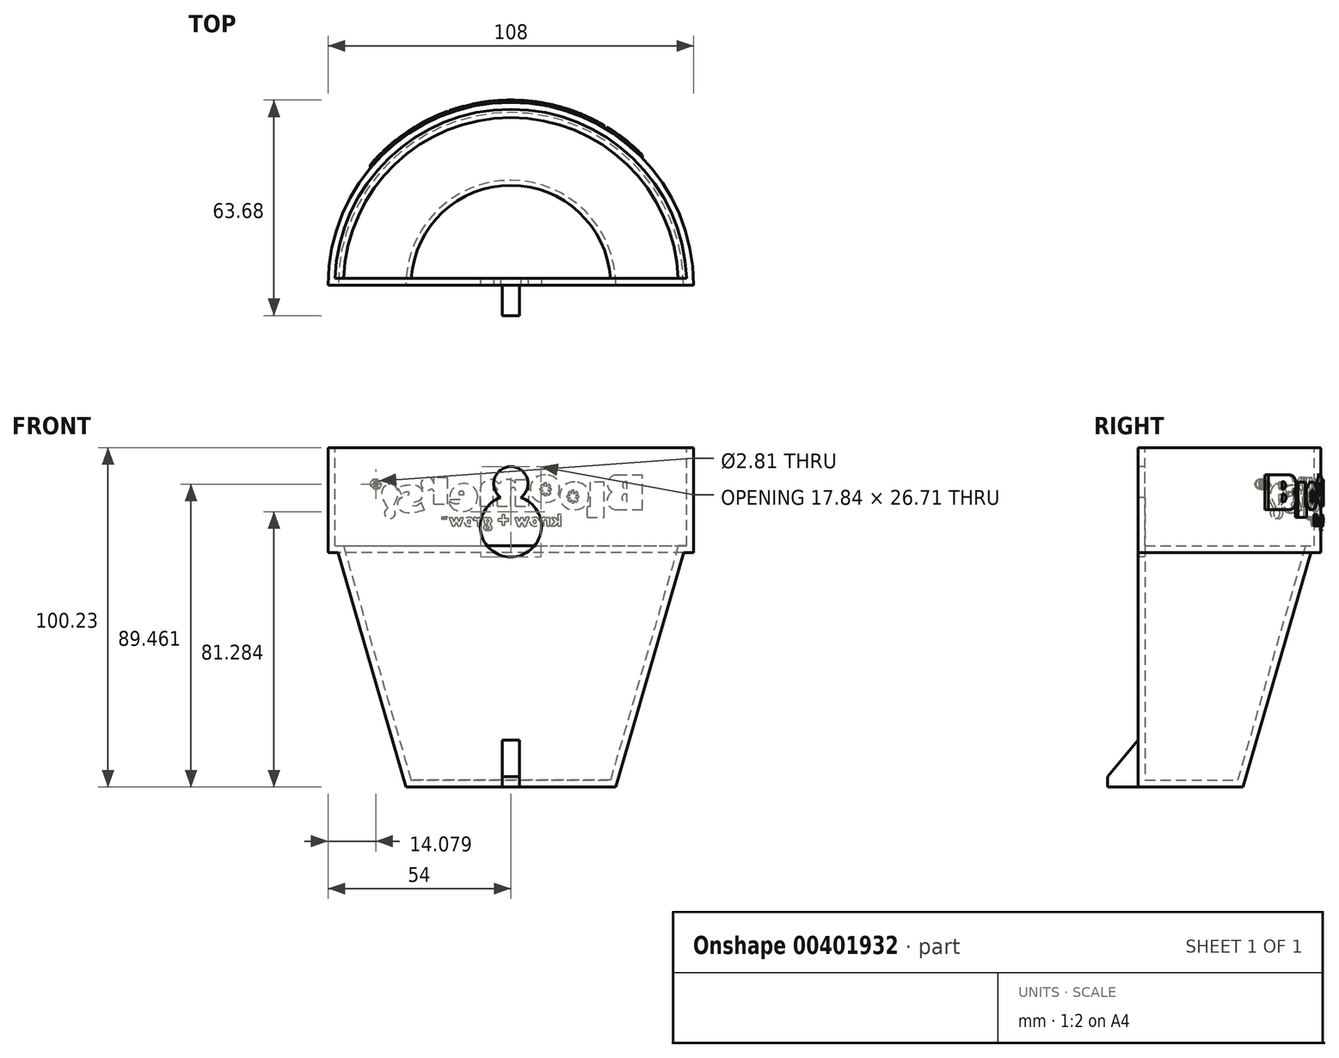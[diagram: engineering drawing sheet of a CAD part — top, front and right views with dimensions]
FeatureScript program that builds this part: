
annotation { "Feature Type Name" : "Feature", "Feature Type Description" : "" }
export const myFeature = defineFeature(function(context is Context, id is Id, definition is map)
    precondition{}
    {
        {
            var Q0;
            Q0=qCreatedBy(makeId("Front.planeOp"),FACE);
            var sketch = newSketch(context, id + "F0", { "sketchPlane" : qUnion([Q0])});
            skLineSegment(sketch, "E0", {"start": v(0, 49.42) * mm, "end": v(-54, 49.42) * mm});
            skLineSegment(sketch, "E1", {"start": v(-54, 49.42) * mm, "end": v(-54, 18.42) * mm});
            skLineSegment(sketch, "E2", {"start": v(0, -50.8) * mm, "end": v(-31, -50.8) * mm});
            skLineSegment(sketch, "E3", {"start": v(-54, 18.42) * mm, "end": v(-51, 18.42) * mm});
            skLineSegment(sketch, "E4", {"start": v(0, 49.42) * mm, "end": v(0, -50.8) * mm});
            skLineSegment(sketch, "E5", {"start": v(-51, 18.42) * mm, "end": v(-31, -50.8) * mm});
            skLineSegment(sketch, "E6.MirrorCS", {"start": v(0, 49.42) * mm, "end": v(54, 49.42) * mm});
            skLineSegment(sketch, "E7.MirrorCS", {"start": v(54, 49.42) * mm, "end": v(54, 18.42) * mm});
            skLineSegment(sketch, "E8.MirrorCS", {"start": v(54, 18.42) * mm, "end": v(51, 18.42) * mm});
            skLineSegment(sketch, "E9.MirrorCS", {"start": v(51, 18.42) * mm, "end": v(31, -50.8) * mm});
            skLineSegment(sketch, "E10.MirrorCS", {"start": v(0, -50.8) * mm, "end": v(31, -50.8) * mm});
            skSolve(sketch);
        }
        {
            var Q0;
            {var subQ0=sQuery(id+"F0.wireOp",EDGE,"E3");Q0=makeQuery(id+"F0.imprint","IMPRINT",FACE,{"disambiguationData":[TD([[makeQuery(id+"F0.imprint","IMPRINT",EDGE,{"derivedFrom":subQ0}),1.0]])]});}
            var Q1;
            {var subQ1=sQuery(id+"F0.wireOp",EDGE,"E0");Q1=makeQuery(id+"F0.imprint","IMPRINT",FACE,{"disambiguationData":[TD([[makeQuery(id+"F0.imprint","IMPRINT",EDGE,{"derivedFrom":subQ1}),1.0]])]});}
            var Q2;
            Q2=makeQuery(id+"F0.imprint","IMPRINT",FACE,{"disambiguationData":[TD([[makeQuery(id+"F0.imprint","IMPRINT",EDGE,{"derivedFrom":sQuery(id+"F0.wireOp",EDGE,"Kfnrekvc-ZjTY-c2iQ-cK4z-hKnBe4uEAVNk")}),1.0]])]});
            var Q3;
            Q3=sQuery(id+"F0.wireOp",EDGE,"E4");
            revolve(context, id + "F1", {"entities" : qUnion([Q0, Q1, Q2]), "axis" : qUnion([Q3]), "revolveType" : RevolveType.ONE_DIRECTION, "angle" : 180 * degree});
        }
        {
            var Q0;
            Q0=makeQuery(id+"FK2OT3XlAi37Aaq_1.splitOp","SPLIT",FACE,{"derivedFrom":makeQuery(id+"F1.opRevolve","SWEPT_FACE",FACE,{"disambiguationData":[OSD([sQuery(id+"F0.wireOp",EDGE,"E0")])]}),"isFromBackBody":true});
            shell(context, id + "F2", {"entities" : qUnion([Q0]), "thickness" : 2 * mm});
        }
        {
            var Q0;
            Q0=qCreatedBy(makeId("Front.planeOp"),FACE);
            var sketch = newSketch(context, id + "F3", { "sketchPlane" : qUnion([Q0])});
            skLineSegment(sketch, "E11.bottom", {"start": v(-2.5, -35.8) * mm, "end": v(2.5, -35.8) * mm});
            skLineSegment(sketch, "E11.top", {"start": v(-2.5, -50.8) * mm, "end": v(2.5, -50.8) * mm});
            skLineSegment(sketch, "E11.left", {"start": v(-2.5, -35.8) * mm, "end": v(-2.5, -50.8) * mm});
            skLineSegment(sketch, "E11.right", {"start": v(2.5, -35.8) * mm, "end": v(2.5, -50.8) * mm});
            skPoint(sketch, "E11.middle", {"position": v(0, -43.3) * mm});
            skSolve(sketch);
        }
        {
            var Q0;
            Q0=qSketchRegion(id+"F3",true);
            extrude(context, id + "F4", {"entities" : qUnion([Q0]), "operationType" : NewBodyOperationType.ADD, "depth" : 9 * mm});
        }
        {
            var Q0;
            Q0=qCreatedBy(makeId("Front.planeOp"),FACE);
            var sketch = newSketch(context, id + "F5", { "sketchPlane" : qUnion([Q0])});
            skCircle(sketch, "E12", {"center": v(0, 38.78) * mm, "radius": 5.05 * mm});
            skCircle(sketch, "E13", {"center": v(0, 26.17) * mm, "radius": 9.05 * mm});
            skSolve(sketch);
        }
        {
            var Q0;
            {var subQ0=sQuery(id+"F5.wireOp",EDGE,"E13");var subQ1=sQuery(id+"F5.wireOp",EDGE,"E12");var subQ2=makeQuery(id+"F5.imprint","INTERSECT",VERTEX,{"disambiguationData":[OD(0.0)],"derivedFrom":[subQ1,subQ0]});Q0=makeQuery(id+"F5.imprint","IMPRINT",FACE,{"disambiguationData":[TD([[makeQuery(id+"F5.imprint","IMPRINT",EDGE,{"disambiguationData":[TD([[subQ2,1.0]])],"derivedFrom":subQ1}),1.0]])]});}
            var Q1;
            {var subQ0=sQuery(id+"F5.wireOp",EDGE,"E13");var subQ1=sQuery(id+"F5.wireOp",EDGE,"E12");var subQ2=makeQuery(id+"F5.imprint","INTERSECT",VERTEX,{"disambiguationData":[OD(0.0)],"derivedFrom":[subQ1,subQ0]});Q1=makeQuery(id+"F5.imprint","IMPRINT",FACE,{"disambiguationData":[TD([[makeQuery(id+"F5.imprint","IMPRINT",EDGE,{"disambiguationData":[TD([[subQ2,-1.0]])],"derivedFrom":subQ1}),-1.0]])]});}
            var Q2;
            {var subQ0=sQuery(id+"F5.wireOp",EDGE,"E13");var subQ1=sQuery(id+"F5.wireOp",EDGE,"E12");var subQ2=makeQuery(id+"F5.imprint","INTERSECT",VERTEX,{"disambiguationData":[OD(0.0)],"derivedFrom":[subQ1,subQ0]});Q2=makeQuery(id+"F5.imprint","IMPRINT",FACE,{"disambiguationData":[TD([[makeQuery(id+"F5.imprint","IMPRINT",EDGE,{"disambiguationData":[TD([[subQ2,-1.0]])],"derivedFrom":subQ1}),1.0]])]});}
            var Q3;
            Q3=sQuery(id+"F5.wireOp",EDGE,"E12");
            var Q4;
            Q4=sQuery(id+"F5.wireOp",EDGE,"E13");
            extrude(context, id + "F6", {"entities" : qUnion([Q0, Q1, Q2]), "operationType" : NewBodyOperationType.REMOVE, "surfaceEntities" : qUnion([Q3, Q4]), "oppositeDirection" : true, "depth" : 10 * mm});
        }
        {
            var Q0;
            Q0=makeQuery(id+"F4.opExtrude","CAP_EDGE",EDGE,{"disambiguationData":[OSD([sQuery(id+"F3.wireOp",EDGE,"E11.bottom")])],"isStart":false});
            chamfer(context, id + "F7", {"entities" : qUnion([Q0]), "chamferType" : ChamferType.OFFSET_ANGLE, "width" : 10 * mm, "oppositeDirection" : false, "angle" : 50 * degree, "tangentPropagation" : true});
        }
        {
            var Q0;
            Q0=makeQuery(id+"F2.opShell","OFFSET_FACE",FACE,{"disambiguationData":[OSD([sQuery(id+"F0.wireOp",EDGE,"E0"),sQuery(id+"F0.wireOp",EDGE,"E1"),sQuery(id+"F0.wireOp",EDGE,"E2"),sQuery(id+"F0.wireOp",EDGE,"E3"),sQuery(id+"F0.wireOp",EDGE,"E4"),sQuery(id+"F0.wireOp",EDGE,"E5")])]});
            cPlane(context, id + "F8", {"entities" : qUnion([Q0]), "cplaneType" : CPlaneType.OFFSET, "offset" : 52.7 * mm, "width" : 150 * mm, "height" : 150 * mm});
        }
        {
            var Q0;
            Q0=qCreatedBy(id+"F8.planeOp",FACE);
            var sketch = newSketch(context, id + "F9", { "sketchPlane" : qUnion([Q0])});
            skLineSegment(sketch, "E14", {"start": v(-38.93, 41.35) * mm, "end": v(-38.93, 31.1) * mm});
            skLineSegment(sketch, "E15", {"start": v(-38.93, 31.1) * mm, "end": v(-31.26, 31.1) * mm});
            skLineSegment(sketch, "E16", {"start": v(-38.93, 41.35) * mm, "end": v(-31.26, 41.35) * mm});
            skArc(sketch, "E17", {"start": v(-29.86, 36.3) * mm, "mid": v(-28.64, 39.36) * mm, "end": v(-31.26, 41.35) * mm});
            skArc(sketch, "E18", {"start": v(-31.26, 31.1) * mm, "mid": v(-28.56, 33.17) * mm, "end": v(-29.86, 36.3) * mm});
            skLineSegment(sketch, "E19", {"start": v(-34.3, 39.39) * mm, "end": v(-34.3, 37.24) * mm});
            skArc(sketch, "E20", {"start": v(-34.3, 37.24) * mm, "mid": v(-33, 38.32) * mm, "end": v(-34.3, 39.39) * mm});
            skArc(sketch, "E21", {"start": v(-34.3, 33.47) * mm, "mid": v(-32.82, 34.59) * mm, "end": v(-34.3, 35.7) * mm});
            skLineSegment(sketch, "E22.trimOffspring", {"start": v(-34.3, 35.7) * mm, "end": v(-34.3, 33.47) * mm});
            skLineSegment(sketch, "E23", {"start": v(-27.58, 39.2) * mm, "end": v(-27.58, 28.9) * mm});
            skLineSegment(sketch, "E24", {"start": v(-27.58, 28.9) * mm, "end": v(-22.58, 28.9) * mm});
            skLineSegment(sketch, "E25", {"start": v(-22.58, 28.9) * mm, "end": v(-22.58, 31.98) * mm});
            skLineSegment(sketch, "E26", {"start": v(-22.58, 31.98) * mm, "end": v(-23.52, 31.98) * mm});
            skLineSegment(sketch, "E27", {"start": v(-23.52, 31.98) * mm, "end": v(-23.52, 39.2) * mm});
            skLineSegment(sketch, "E28", {"start": v(-23.52, 39.2) * mm, "end": v(-27.58, 39.2) * mm});
            skFitSpline(sketch, "E29", {"points": [v(-18.97, 39.3) * mm, v(-20.87, 38.92) * mm, v(-22.46, 37.44) * mm, v(-22.99, 35.82) * mm, v(-22.97, 34.09) * mm, v(-22.03, 32.34) * mm, v(-20.21, 31.27) * mm, v(-18.57, 31.14) * mm, v(-16.6, 31.5) * mm, v(-14.9, 33.15) * mm, v(-14.42, 35.37) * mm, v(-14.96, 37.3) * mm, v(-16.45, 38.75) * mm, v(-18.2, 39.28) * mm, v(-18.97, 39.3) * mm]});
            skLineSegment(sketch, "E30.bottom", {"start": v(-18.65, 36.9) * mm, "end": v(-18, 36.9) * mm});
            skLineSegment(sketch, "E30.top", {"start": v(-18.65, 33.13) * mm, "end": v(-18, 33.13) * mm});
            skLineSegment(sketch, "E30.left", {"start": v(-18.65, 36.9) * mm, "end": v(-18.65, 35.74) * mm});
            skLineSegment(sketch, "E30.right", {"start": v(-18, 36.9) * mm, "end": v(-18, 35.82) * mm});
            skLineSegment(sketch, "E31.bottom", {"start": v(-20.04, 35.3) * mm, "end": v(-19.23, 35.3) * mm});
            skLineSegment(sketch, "E31.top", {"start": v(-20.04, 34.7) * mm, "end": v(-19.05, 34.7) * mm});
            skLineSegment(sketch, "E31.left", {"start": v(-20.04, 35.3) * mm, "end": v(-20.04, 34.7) * mm});
            skLineSegment(sketch, "E31.right", {"start": v(-16.69, 35.3) * mm, "end": v(-16.69, 34.7) * mm});
            skLineSegment(sketch, "E32", {"start": v(-19.87, 35.97) * mm, "end": v(-19.23, 35.3) * mm});
            skLineSegment(sketch, "E33", {"start": v(-17.4, 33.43) * mm, "end": v(-16.88, 33.92) * mm});
            skLineSegment(sketch, "E34", {"start": v(-19.35, 36.45) * mm, "end": v(-19.87, 35.97) * mm});
            skLineSegment(sketch, "E35", {"start": v(-19.87, 33.85) * mm, "end": v(-19.25, 33.22) * mm});
            skLineSegment(sketch, "E36", {"start": v(-19.25, 33.22) * mm, "end": v(-18.65, 33.9) * mm});
            skLineSegment(sketch, "E37", {"start": v(-16.84, 35.97) * mm, "end": v(-17.39, 36.45) * mm});
            skLineSegment(sketch, "E38", {"start": v(-17.39, 36.45) * mm, "end": v(-18, 35.82) * mm});
            skLineSegment(sketch, "E39.trimOffspring", {"start": v(-18.65, 35.74) * mm, "end": v(-19.35, 36.45) * mm});
            skLineSegment(sketch, "E40.trimOffspring", {"start": v(-19.05, 34.7) * mm, "end": v(-19.87, 33.85) * mm});
            skLineSegment(sketch, "E41.trimOffspring", {"start": v(-18, 34.04) * mm, "end": v(-17.4, 33.43) * mm});
            skLineSegment(sketch, "E42.trimOffspring", {"start": v(-18.65, 33.9) * mm, "end": v(-18.65, 33.13) * mm});
            skLineSegment(sketch, "E43.trimOffspring", {"start": v(-18, 34.04) * mm, "end": v(-18, 33.13) * mm});
            skLineSegment(sketch, "E44.trimOffspring", {"start": v(-17.42, 35.3) * mm, "end": v(-16.84, 35.97) * mm});
            skLineSegment(sketch, "E45.trimOffspring", {"start": v(-17.42, 35.3) * mm, "end": v(-16.69, 35.3) * mm});
            skLineSegment(sketch, "E46.trimOffspring", {"start": v(-17.65, 34.7) * mm, "end": v(-16.69, 34.7) * mm});
            skFitSpline(sketch, "E47", {"points": [v(-10.3, 41.42) * mm, v(-12.2, 41.04) * mm, v(-13.79, 39.56) * mm, v(-14.32, 37.94) * mm, v(-14.3, 36.2) * mm, v(-13.36, 34.46) * mm, v(-11.55, 33.39) * mm, v(-9.9, 33.26) * mm, v(-7.94, 33.62) * mm, v(-6.23, 35.27) * mm, v(-5.76, 37.49) * mm, v(-6.3, 39.41) * mm, v(-7.79, 40.86) * mm, v(-9.54, 41.4) * mm, v(-10.3, 41.42) * mm]});
            skLineSegment(sketch, "E48", {"start": v(-17.65, 34.7) * mm, "end": v(-16.88, 33.92) * mm});
            skLineSegment(sketch, "E49.bottom", {"start": v(-10.58, 39.06) * mm, "end": v(-9.92, 39.06) * mm});
            skLineSegment(sketch, "E49.top", {"start": v(-10.58, 35.28) * mm, "end": v(-9.92, 35.28) * mm});
            skLineSegment(sketch, "E49.left", {"start": v(-10.58, 39.06) * mm, "end": v(-10.58, 37.9) * mm});
            skLineSegment(sketch, "E49.right", {"start": v(-9.92, 39.06) * mm, "end": v(-9.92, 37.97) * mm});
            skLineSegment(sketch, "E50.bottom", {"start": v(-11.97, 37.46) * mm, "end": v(-11.15, 37.46) * mm});
            skLineSegment(sketch, "E50.top", {"start": v(-11.97, 36.86) * mm, "end": v(-10.98, 36.86) * mm});
            skLineSegment(sketch, "E50.left", {"start": v(-11.97, 37.46) * mm, "end": v(-11.97, 36.86) * mm});
            skLineSegment(sketch, "E50.right", {"start": v(-8.61, 37.46) * mm, "end": v(-8.61, 36.86) * mm});
            skLineSegment(sketch, "E51", {"start": v(-11.8, 38.12) * mm, "end": v(-11.15, 37.46) * mm});
            skLineSegment(sketch, "E52", {"start": v(-9.32, 35.58) * mm, "end": v(-8.81, 36.08) * mm});
            skLineSegment(sketch, "E53", {"start": v(-11.27, 38.6) * mm, "end": v(-11.8, 38.12) * mm});
            skLineSegment(sketch, "E54", {"start": v(-11.8, 36) * mm, "end": v(-11.18, 35.37) * mm});
            skLineSegment(sketch, "E55", {"start": v(-11.18, 35.37) * mm, "end": v(-10.58, 36.05) * mm});
            skLineSegment(sketch, "E56", {"start": v(-8.76, 38.12) * mm, "end": v(-9.31, 38.6) * mm});
            skLineSegment(sketch, "E57", {"start": v(-9.31, 38.6) * mm, "end": v(-9.92, 37.97) * mm});
            skLineSegment(sketch, "E58.trimOffspring", {"start": v(-10.58, 37.9) * mm, "end": v(-11.27, 38.6) * mm});
            skLineSegment(sketch, "E59.trimOffspring", {"start": v(-10.98, 36.86) * mm, "end": v(-11.8, 36) * mm});
            skLineSegment(sketch, "E60.trimOffspring", {"start": v(-9.92, 36.2) * mm, "end": v(-9.32, 35.58) * mm});
            skLineSegment(sketch, "E61.trimOffspring", {"start": v(-10.58, 36.05) * mm, "end": v(-10.58, 35.28) * mm});
            skLineSegment(sketch, "E62.trimOffspring", {"start": v(-9.92, 36.2) * mm, "end": v(-9.92, 35.28) * mm});
            skLineSegment(sketch, "E63.trimOffspring", {"start": v(-9.34, 37.46) * mm, "end": v(-8.76, 38.12) * mm});
            skLineSegment(sketch, "E64.trimOffspring", {"start": v(-9.34, 37.46) * mm, "end": v(-8.61, 37.46) * mm});
            skLineSegment(sketch, "E65.trimOffspring", {"start": v(-9.58, 36.86) * mm, "end": v(-8.61, 36.86) * mm});
            skLineSegment(sketch, "E66", {"start": v(-9.58, 36.86) * mm, "end": v(-8.81, 36.08) * mm});
            skLineSegment(sketch, "E67", {"start": v(-5.38, 32.17) * mm, "end": v(-5.38, 39.97) * mm});
            skLineSegment(sketch, "E68", {"start": v(-5.38, 39.97) * mm, "end": v(-1.39, 39.97) * mm});
            skLineSegment(sketch, "E69", {"start": v(-1.39, 39.97) * mm, "end": v(-1.39, 39) * mm});
            skLineSegment(sketch, "E70", {"start": v(-5.38, 32.17) * mm, "end": v(-1.38, 32.17) * mm});
            skLineSegment(sketch, "E71", {"start": v(-1.38, 32.17) * mm, "end": v(-1.38, 36.98) * mm});
            skLineSegment(sketch, "E72", {"start": v(0, 36.98) * mm, "end": v(0, 32.17) * mm});
            skLineSegment(sketch, "E73", {"start": v(0, 32.17) * mm, "end": v(3.95, 32.17) * mm});
            skLineSegment(sketch, "E74", {"start": v(3.95, 32.17) * mm, "end": v(3.95, 36.98) * mm});
            skLineSegment(sketch, "E75", {"start": v(5.25, 36.98) * mm, "end": v(5.25, 32.17) * mm});
            skLineSegment(sketch, "E76", {"start": v(5.25, 32.17) * mm, "end": v(9.02, 32.17) * mm});
            skLineSegment(sketch, "E77", {"start": v(9.02, 32.17) * mm, "end": v(9.02, 36.98) * mm});
            skArc(sketch, "E78", {"start": v(5.25, 36.98) * mm, "mid": v(4.6, 37.63) * mm, "end": v(3.95, 36.98) * mm});
            skArc(sketch, "E79", {"start": v(0, 36.98) * mm, "mid": v(-0.69, 37.67) * mm, "end": v(-1.38, 36.98) * mm});
            skArc(sketch, "E80", {"start": v(3.53, 38.66) * mm, "mid": v(1.15, 40.01) * mm, "end": v(-1.39, 39) * mm});
            skArc(sketch, "E81", {"start": v(9.02, 36.98) * mm, "mid": v(6.9, 39.85) * mm, "end": v(3.53, 38.66) * mm});
            skArc(sketch, "E82", {"start": v(13.95, 34.1) * mm, "mid": v(15.9, 32.9) * mm, "end": v(18.03, 33.72) * mm});
            skArc(sketch, "E83", {"start": v(9.77, 35.2) * mm, "mid": v(12.91, 30.78) * mm, "end": v(18.06, 32.5) * mm});
            skArc(sketch, "E84", {"start": v(18.03, 34.17) * mm, "mid": v(14.4, 38.8) * mm, "end": v(9.77, 35.2) * mm});
            skLineSegment(sketch, "E85", {"start": v(13.95, 34.1) * mm, "end": v(18.03, 34.17) * mm});
            skLineSegment(sketch, "E86", {"start": v(13.9, 35.57) * mm, "end": v(15.36, 35.6) * mm});
            skArc(sketch, "E87", {"start": v(15.36, 35.6) * mm, "mid": v(14.6, 36.63) * mm, "end": v(13.9, 35.57) * mm});
            skLineSegment(sketch, "E88", {"start": v(18.03, 33.72) * mm, "end": v(18.06, 32.5) * mm});
            skLineSegment(sketch, "E89", {"start": v(22.73, 38.77) * mm, "end": v(22.73, 40.55) * mm});
            skLineSegment(sketch, "E90", {"start": v(22.73, 40.55) * mm, "end": v(18.72, 40.58) * mm});
            skLineSegment(sketch, "E91", {"start": v(18.72, 40.58) * mm, "end": v(18.72, 32.74) * mm});
            skLineSegment(sketch, "E92", {"start": v(18.72, 32.74) * mm, "end": v(22.7, 32.74) * mm});
            skLineSegment(sketch, "E93", {"start": v(22.7, 32.74) * mm, "end": v(22.7, 36.3) * mm});
            skArc(sketch, "E94", {"start": v(23.94, 36.98) * mm, "mid": v(26.24, 39.84) * mm, "end": v(22.73, 38.77) * mm});
            skArc(sketch, "E95", {"start": v(23.94, 36.98) * mm, "mid": v(23.11, 37) * mm, "end": v(22.7, 36.3) * mm});
            skLineSegment(sketch, "E96", {"start": v(33.3, 37.45) * mm, "end": v(32.27, 35.62) * mm});
            skFitSpline(sketch, "E97", {"points": [v(33.3, 37.45) * mm, v(32.36, 37.96) * mm, v(31.25, 38.2) * mm, v(30.16, 38.3) * mm, v(28.65, 38.26) * mm, v(27.14, 37.83) * mm, v(26.29, 37.06) * mm, v(25.86, 36.05) * mm, v(26.07, 34.84) * mm, v(26.79, 33.99) * mm, v(28.33, 33.35) * mm, v(29.12, 33.1) * mm, v(29.36, 32.85) * mm, v(29.3, 32.47) * mm, v(29, 32.12) * mm, v(28.48, 32.1) * mm, v(27.57, 32.38) * mm, v(26.88, 32.96) * mm, v(26.6, 33.22) * mm, v(26.49, 33.3) * mm], "startDerivative": vector(-15.65, 9.87) * mm, "endDerivative": vector(-4.84, 3.4) * mm});
            skFitSpline(sketch, "E98", {"points": [v(32.27, 35.62) * mm, v(31.94, 35.79) * mm, v(31.56, 36.06) * mm, v(31.13, 36.28) * mm, v(30.73, 36.4) * mm, v(30.1, 36.28) * mm, v(29.89, 35.88) * mm, v(30.08, 35.62) * mm, v(30.64, 35.32) * mm, v(31.42, 35.1) * mm, v(32.1, 34.87) * mm, v(32.63, 34.52) * mm, v(33.07, 34.09) * mm, v(33.37, 33.46) * mm, v(33.46, 33) * mm, v(33.46, 32.48) * mm, v(33.31, 31.72) * mm, v(32.8, 31.07) * mm, v(32.27, 30.71) * mm, v(31.46, 30.26) * mm, v(30.44, 30.1) * mm, v(29.25, 30.17) * mm, v(28.56, 30.21) * mm, v(27.53, 30.4) * mm, v(26.65, 30.67) * mm, v(26.13, 30.83) * mm, v(25.52, 31) * mm, v(24, 31.52) * mm], "startDerivative": vector(-12.22, 5.14) * mm, "endDerivative": vector(-29.8, 10.92) * mm});
            skLineSegment(sketch, "E99", {"start": v(26.49, 33.3) * mm, "end": v(25.52, 31) * mm});
            skFitSpline(sketch, "E100", {"points": [v(35.16, 31.53) * mm, v(34.54, 32.68) * mm, v(33.94, 33.8) * mm, v(33.6, 34.86) * mm, v(33.49, 36.06) * mm, v(33.7, 37.34) * mm, v(34.55, 38.4) * mm, v(35.36, 38.83) * mm, v(36.02, 38.89) * mm, v(36.86, 38.44) * mm, v(37.6, 37.54) * mm, v(38.02, 36.55) * mm, v(37.98, 35.4) * mm, v(37.68, 34.14) * mm, v(37.17, 33.21) * mm, v(36.7, 32.27) * mm, v(36.3, 31.56) * mm, v(36.34, 31.34) * mm], "startDerivative": vector(-9.25, 17.51) * mm, "endDerivative": vector(7.08, -5.7) * mm});
            skFitSpline(sketch, "E101", {"points": [v(35.16, 31.53) * mm, v(34.67, 31.23) * mm, v(34.3, 30.83) * mm, v(34.1, 30) * mm, v(34.28, 29.4) * mm, v(34.62, 28.94) * mm, v(35.02, 28.64) * mm, v(35.5, 28.5) * mm, v(36.33, 28.63) * mm, v(37.12, 29.37) * mm, v(37.32, 30.35) * mm, v(37.03, 31) * mm, v(36.66, 31.33) * mm, v(36.3, 31.56) * mm], "startDerivative": vector(-7.2, -4.04) * mm, "endDerivative": vector(-5.92, 3.66) * mm});
            skLineSegment(sketch, "E102", {"start": v(-13.86, 29.67) * mm, "end": v(-14.85, 29.67) * mm});
            skLineSegment(sketch, "E103", {"start": v(-14.85, 29.67) * mm, "end": v(-14.85, 26.29) * mm});
            skLineSegment(sketch, "E104", {"start": v(-14.85, 26.29) * mm, "end": v(-13.95, 26.29) * mm});
            skLineSegment(sketch, "E105", {"start": v(-13.95, 26.29) * mm, "end": v(-13.95, 27.28) * mm});
            skLineSegment(sketch, "E106", {"start": v(-13.95, 27.28) * mm, "end": v(-13.01, 26.29) * mm});
            skLineSegment(sketch, "E107", {"start": v(-13.01, 26.29) * mm, "end": v(-11.85, 26.29) * mm});
            skLineSegment(sketch, "E108", {"start": v(-11.85, 26.29) * mm, "end": v(-12.9, 27.58) * mm});
            skLineSegment(sketch, "E109", {"start": v(-12.9, 27.58) * mm, "end": v(-11.98, 28.72) * mm});
            skLineSegment(sketch, "E110", {"start": v(-11.98, 28.72) * mm, "end": v(-13.1, 28.72) * mm});
            skLineSegment(sketch, "E111", {"start": v(-13.1, 28.72) * mm, "end": v(-13.95, 27.88) * mm});
            skLineSegment(sketch, "E112", {"start": v(-13.95, 27.88) * mm, "end": v(-13.86, 29.67) * mm});
            skLineSegment(sketch, "E113", {"start": v(-11.59, 26.29) * mm, "end": v(-10.62, 26.29) * mm});
            skLineSegment(sketch, "E114", {"start": v(-10.62, 26.29) * mm, "end": v(-10.62, 27.77) * mm});
            skLineSegment(sketch, "E115", {"start": v(-9.77, 27.88) * mm, "end": v(-9.77, 26.29) * mm});
            skLineSegment(sketch, "E116", {"start": v(-9.77, 26.29) * mm, "end": v(-8.9, 26.29) * mm});
            skLineSegment(sketch, "E117", {"start": v(-8.9, 26.29) * mm, "end": v(-8.95, 28.42) * mm});
            skLineSegment(sketch, "E118", {"start": v(-10.49, 28.6) * mm, "end": v(-10.62, 28.6) * mm});
            skLineSegment(sketch, "E119", {"start": v(-10.62, 28.6) * mm, "end": v(-10.62, 28.76) * mm});
            skLineSegment(sketch, "E120", {"start": v(-10.62, 28.76) * mm, "end": v(-11.61, 28.76) * mm});
            skLineSegment(sketch, "E121", {"start": v(-11.61, 28.76) * mm, "end": v(-11.59, 26.29) * mm});
            skEllipse(sketch, "E122", {"center": v(-7.04, 27.54) * mm, "majorRadius": 0.56 * mm, "minorRadius": 0.44 * mm, "majorAxis": v(0, -1)});
            skEllipse(sketch, "E123", {"center": v(-7.04, 27.54) * mm, "majorRadius": 1.33 * mm, "minorRadius": 1.47 * mm, "majorAxis": v(0.05, -1)});
            skLineSegment(sketch, "E124", {"start": v(-4.42, 28.79) * mm, "end": v(-5.45, 28.79) * mm});
            skLineSegment(sketch, "E125", {"start": v(-5.45, 28.79) * mm, "end": v(-4.45, 26.23) * mm});
            skLineSegment(sketch, "E126", {"start": v(-4.45, 26.23) * mm, "end": v(-3.77, 26.23) * mm});
            skLineSegment(sketch, "E127", {"start": v(-3.77, 26.23) * mm, "end": v(-3.28, 27.38) * mm});
            skLineSegment(sketch, "E128", {"start": v(-3.28, 27.38) * mm, "end": v(-2.82, 26.22) * mm});
            skLineSegment(sketch, "E129", {"start": v(-2.82, 26.22) * mm, "end": v(-2.1, 26.22) * mm});
            skLineSegment(sketch, "E130", {"start": v(-2.1, 26.22) * mm, "end": v(-1.1, 28.75) * mm});
            skLineSegment(sketch, "E131", {"start": v(-1.1, 28.75) * mm, "end": v(-2.15, 28.75) * mm});
            skLineSegment(sketch, "E132", {"start": v(-2.15, 28.75) * mm, "end": v(-2.48, 27.64) * mm});
            skLineSegment(sketch, "E133", {"start": v(-2.48, 27.64) * mm, "end": v(-2.9, 28.75) * mm});
            skLineSegment(sketch, "E134", {"start": v(-2.9, 28.75) * mm, "end": v(-3.65, 28.75) * mm});
            skLineSegment(sketch, "E135", {"start": v(-3.65, 28.75) * mm, "end": v(-4.02, 27.66) * mm});
            skLineSegment(sketch, "E136", {"start": v(-4.02, 27.66) * mm, "end": v(-4.42, 28.79) * mm});
            skLineSegment(sketch, "E137", {"start": v(2.5, 29.58) * mm, "end": v(1.8, 29.58) * mm});
            skLineSegment(sketch, "E138", {"start": v(1.8, 29.58) * mm, "end": v(1.8, 28.47) * mm});
            skLineSegment(sketch, "E139", {"start": v(1.8, 28.47) * mm, "end": v(0.59, 28.47) * mm});
            skLineSegment(sketch, "E140", {"start": v(0.59, 28.47) * mm, "end": v(0.59, 27.74) * mm});
            skLineSegment(sketch, "E141", {"start": v(0.59, 27.74) * mm, "end": v(1.77, 27.74) * mm});
            skLineSegment(sketch, "E142", {"start": v(1.77, 27.74) * mm, "end": v(1.77, 26.58) * mm});
            skLineSegment(sketch, "E143", {"start": v(1.77, 26.58) * mm, "end": v(2.5, 26.58) * mm});
            skLineSegment(sketch, "E144", {"start": v(2.5, 26.58) * mm, "end": v(2.5, 27.74) * mm});
            skLineSegment(sketch, "E145", {"start": v(2.5, 27.74) * mm, "end": v(3.63, 27.74) * mm});
            skLineSegment(sketch, "E146", {"start": v(3.63, 27.74) * mm, "end": v(3.63, 28.45) * mm});
            skLineSegment(sketch, "E147", {"start": v(3.63, 28.45) * mm, "end": v(2.5, 28.45) * mm});
            skLineSegment(sketch, "E148", {"start": v(2.5, 28.45) * mm, "end": v(2.5, 29.58) * mm});
            skEllipse(sketch, "E149", {"center": v(12.37, 27.5) * mm, "majorRadius": 0.56 * mm, "minorRadius": 0.47 * mm, "majorAxis": v(0, -1)});
            skEllipse(sketch, "E150", {"center": v(12.37, 27.5) * mm, "majorRadius": 1.38 * mm, "minorRadius": 1.44 * mm, "majorAxis": v(0, -1)});
            skEllipse(sketch, "E151", {"center": v(6.82, 27.81) * mm, "majorRadius": 0.35 * mm, "minorRadius": 0.38 * mm, "majorAxis": v(0, -1)});
            skEllipse(sketch, "E152", {"center": v(6.86, 25.77) * mm, "majorRadius": 0.5 * mm, "minorRadius": 0.27 * mm, "majorAxis": v(1, 0)});
            skLineSegment(sketch, "E153", {"start": v(9.75, 28.76) * mm, "end": v(8.72, 28.76) * mm});
            skLineSegment(sketch, "E154", {"start": v(8.72, 28.76) * mm, "end": v(8.72, 26.23) * mm});
            skLineSegment(sketch, "E155", {"start": v(8.72, 26.23) * mm, "end": v(9.77, 26.23) * mm});
            skLineSegment(sketch, "E156", {"start": v(9.77, 26.23) * mm, "end": v(9.77, 27.57) * mm});
            skLineSegment(sketch, "E157", {"start": v(16.42, 28.76) * mm, "end": v(15.75, 28.76) * mm});
            skLineSegment(sketch, "E158", {"start": v(15.75, 28.76) * mm, "end": v(15.33, 27.62) * mm});
            skLineSegment(sketch, "E159", {"start": v(15.33, 27.62) * mm, "end": v(14.91, 28.77) * mm});
            skLineSegment(sketch, "E160", {"start": v(14.91, 28.77) * mm, "end": v(14, 28.77) * mm});
            skLineSegment(sketch, "E161", {"start": v(14, 28.77) * mm, "end": v(14.91, 26.25) * mm});
            skLineSegment(sketch, "E162", {"start": v(14.91, 26.25) * mm, "end": v(15.58, 26.25) * mm});
            skLineSegment(sketch, "E163", {"start": v(15.58, 26.25) * mm, "end": v(16.06, 27.35) * mm});
            skLineSegment(sketch, "E164", {"start": v(16.06, 27.35) * mm, "end": v(16.6, 26.24) * mm});
            skLineSegment(sketch, "E165", {"start": v(16.6, 26.24) * mm, "end": v(17.25, 26.24) * mm});
            skLineSegment(sketch, "E166", {"start": v(17.25, 26.24) * mm, "end": v(18.26, 28.77) * mm});
            skLineSegment(sketch, "E167", {"start": v(18.26, 28.77) * mm, "end": v(17.24, 28.77) * mm});
            skLineSegment(sketch, "E168", {"start": v(17.24, 28.77) * mm, "end": v(16.82, 27.63) * mm});
            skLineSegment(sketch, "E169", {"start": v(16.82, 27.63) * mm, "end": v(16.42, 28.76) * mm});
            skArc(sketch, "E170", {"start": v(-9.77, 27.88) * mm, "mid": v(-10.23, 28.08) * mm, "end": v(-10.62, 27.77) * mm});
            skArc(sketch, "E171", {"start": v(-8.95, 28.42) * mm, "mid": v(-9.68, 28.85) * mm, "end": v(-10.49, 28.6) * mm});
            skLineSegment(sketch, "E172", {"start": v(9.75, 28.76) * mm, "end": v(9.75, 28.32) * mm});
            skLineSegment(sketch, "E173", {"start": v(10.97, 28.72) * mm, "end": v(10.69, 27.75) * mm});
            skArc(sketch, "E174", {"start": v(10.97, 28.72) * mm, "mid": v(10.29, 28.75) * mm, "end": v(9.75, 28.32) * mm});
            skArc(sketch, "E175", {"start": v(10.69, 27.75) * mm, "mid": v(10.2, 27.84) * mm, "end": v(9.77, 27.57) * mm});
            skLineSegment(sketch, "E176", {"start": v(8.25, 28.14) * mm, "end": v(8.25, 28.77) * mm});
            skLineSegment(sketch, "E177", {"start": v(8.25, 28.77) * mm, "end": v(6.33, 28.77) * mm});
            skArc(sketch, "E178", {"start": v(6.33, 28.77) * mm, "mid": v(5.61, 27.95) * mm, "end": v(6.19, 27.03) * mm});
            skArc(sketch, "E179", {"start": v(6.83, 26.9) * mm, "mid": v(7.8, 27.15) * mm, "end": v(7.96, 28.14) * mm});
            skLineSegment(sketch, "E180", {"start": v(7.96, 28.14) * mm, "end": v(8.25, 28.14) * mm});
            skLineSegment(sketch, "E181", {"start": v(6.83, 26.9) * mm, "end": v(6.83, 26.6) * mm});
            skLineSegment(sketch, "E182", {"start": v(6.83, 26.6) * mm, "end": v(7.57, 26.6) * mm});
            skArc(sketch, "E183", {"start": v(6.19, 27.03) * mm, "mid": v(5.96, 26.73) * mm, "end": v(6.04, 26.36) * mm});
            skArc(sketch, "E184", {"start": v(6.04, 26.36) * mm, "mid": v(5.52, 25.75) * mm, "end": v(6.04, 25.14) * mm});
            skArc(sketch, "E185", {"start": v(7.57, 25.14) * mm, "mid": v(8.09, 25.87) * mm, "end": v(7.57, 26.6) * mm});
            skArc(sketch, "E186", {"start": v(6.04, 25.14) * mm, "mid": v(6.8, 25.03) * mm, "end": v(7.57, 25.14) * mm});
            skText(sketch, "E187", { "text": "TM", "fontName": "OpenSans-Regular.ttf"});
            skCircle(sketch, "E188", {"center": v(39.92, 38.65) * mm, "radius": 1.58 * mm});
            skCircle(sketch, "E189", {"center": v(39.92, 38.65) * mm, "radius": 1.4 * mm});
            const initialGuessF9  = {"E187": [0.0186, 0.02816, 1, 0, 0.0009]};
            skSetInitialGuess(sketch, initialGuessF9);
            skSolve(sketch);
        }
        {
            var Q0;
            Q0=qSketchRegion(id+"F9",true);
            extrude(context, id + "F10", {"entities" : qUnion([Q0]), "operationType" : NewBodyOperationType.ADD, "endBound" : BoundingType.UP_TO_NEXT, "oppositeDirection" : true, "depth" : 25 * mm});
        }
        {
            var Q0;
            Q0=qCreatedBy(id+"F8.planeOp",FACE);
            var sketch = newSketch(context, id + "F11", { "sketchPlane" : qUnion([Q0])});
            skText(sketch, "E190", { "text": "R", "fontName": "OpenSans-Regular.ttf"});
            const initialGuessF11  = {"E190": [0.03904, 0.03769, 1, 0, 0.0019]};
            skSetInitialGuess(sketch, initialGuessF11);
            skSolve(sketch);
        }
        {
            var Q0;
            Q0 = qSketchRegion(id + "F11", true);
            extrude(context, id + "F12", {"entities" : qUnion([Q0]), "operationType" : NewBodyOperationType.ADD, "endBound" : BoundingType.UP_TO_NEXT, "oppositeDirection" : true, "depth" : 25 * mm});
        }
        {
            var Q0;
            Q0=makeQuery(id+"F1.opRevolve","SWEPT_FACE",FACE,{"disambiguationData":[OSD([sQuery(id+"F0.wireOp",EDGE,"E0")])]});
            var sketch = newSketch(context, id + "F13", { "sketchPlane" : qUnion([Q0])});
            skCircle(sketch, "E191", {"center": v(0, 0) * mm, "radius": 54.68 * mm});
            skCircle(sketch, "E192", {"center": v(0, 0) * mm, "radius": 73.66 * mm});
            skSolve(sketch);
        }
        {
            var Q0;
            Q0=qSketchRegion(id+"F13",true);
            extrude(context, id + "F14", {"entities" : qUnion([Q0]), "operationType" : NewBodyOperationType.REMOVE, "oppositeDirection" : true, "depth" : 124 * mm});
        }
    });
